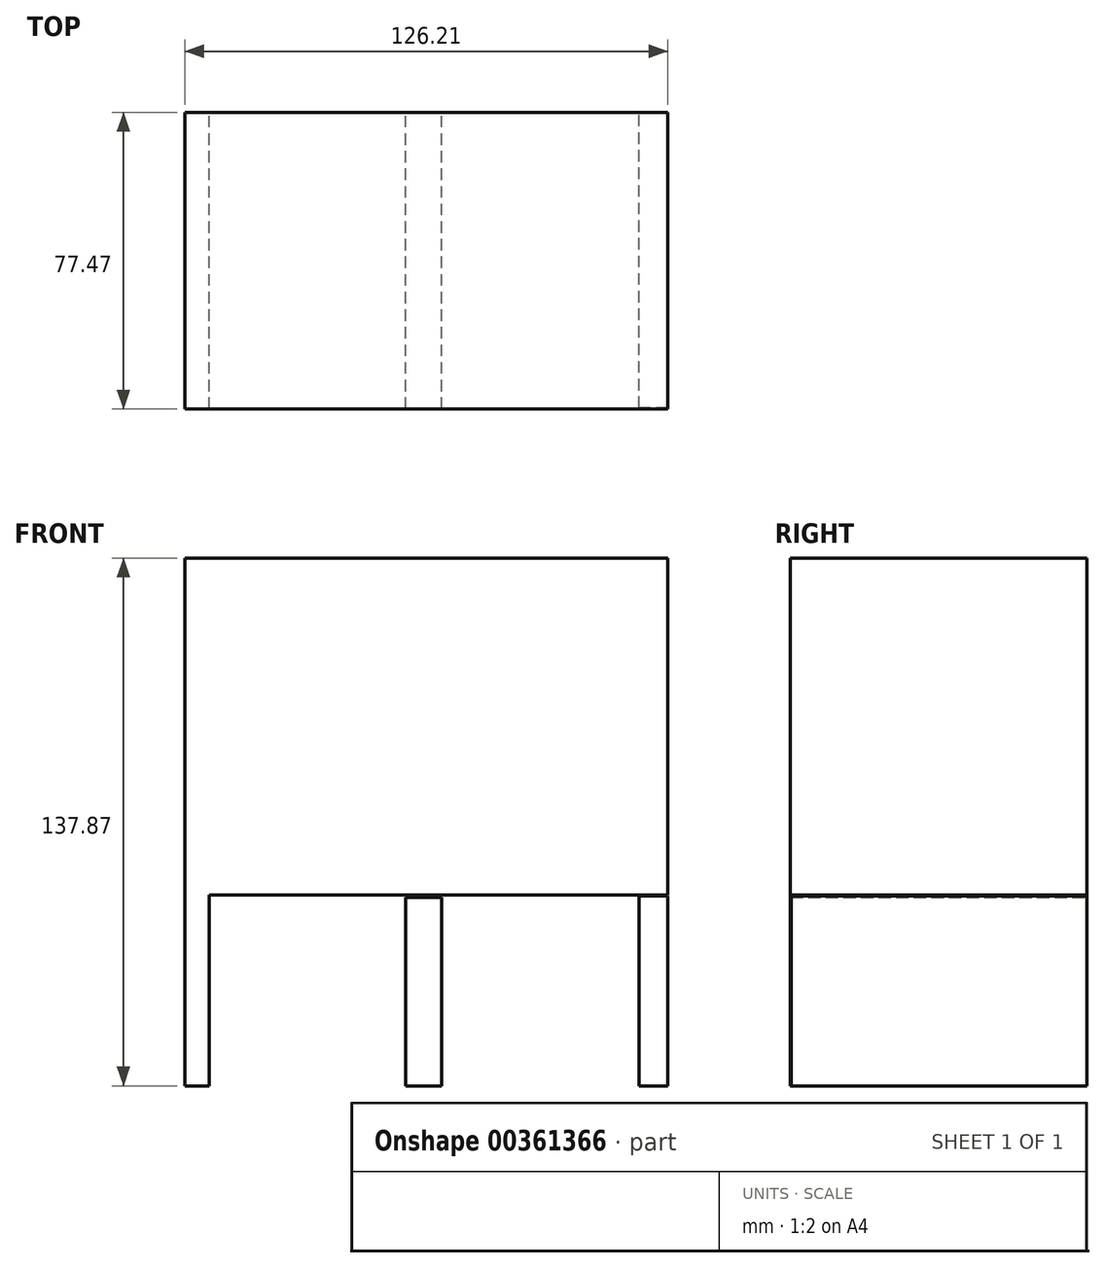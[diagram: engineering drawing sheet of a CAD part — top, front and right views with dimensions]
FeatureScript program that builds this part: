
annotation { "Feature Type Name" : "Feature", "Feature Type Description" : "" }
export const myFeature = defineFeature(function(context is Context, id is Id, definition is map)
    precondition{}
    {
        {
            var Q0;
            Q0=qCreatedBy(makeId("Front.planeOp"),FACE);
            var sketch = newSketch(context, id + "F0", { "sketchPlane" : qUnion([Q0])});
            skLineSegment(sketch, "E0.bottom", {"start": v(-62.38, 61.94) * mm, "end": v(63.83, 61.94) * mm});
            skLineSegment(sketch, "E0.top", {"start": v(-62.38, -26.09) * mm, "end": v(63.83, -26.09) * mm});
            skLineSegment(sketch, "E0.left", {"start": v(-62.38, 61.94) * mm, "end": v(-62.38, -26.09) * mm});
            skLineSegment(sketch, "E0.right", {"start": v(63.83, 61.94) * mm, "end": v(63.83, -26.09) * mm});
            skSolve(sketch);
        }
        {
            var Q0;
            Q0=makeQuery(id+"F0.imprint","IMPRINT",FACE,{"disambiguationData":[TD([[makeQuery(id+"F0.imprint","IMPRINT",EDGE,{"derivedFrom":sQuery(id+"F0.wireOp",EDGE,"E0.bottom")}),-1.0]])]});
            extrude(context, id + "F1", {"entities" : qUnion([Q0]), "depth" : 77.47 * mm});
        }
        {
            var Q0;
            Q0=qCreatedBy(makeId("Front.planeOp"),FACE);
            var sketch = newSketch(context, id + "F2", { "sketchPlane" : qUnion([Q0])});
            skLineSegment(sketch, "E1.bottom", {"start": v(-62.38, -26.09) * mm, "end": v(-55.96, -26.09) * mm});
            skLineSegment(sketch, "E1.top", {"start": v(-62.38, -75.93) * mm, "end": v(-55.96, -75.93) * mm});
            skLineSegment(sketch, "E1.left", {"start": v(-62.38, -26.09) * mm, "end": v(-62.38, -75.93) * mm});
            skLineSegment(sketch, "E1.right", {"start": v(-55.96, -26.09) * mm, "end": v(-55.96, -75.93) * mm});
            skLineSegment(sketch, "E2.bottom", {"start": v(63.83, -26.38) * mm, "end": v(56.25, -26.38) * mm});
            skLineSegment(sketch, "E2.top", {"start": v(63.83, -75.93) * mm, "end": v(56.25, -75.93) * mm});
            skLineSegment(sketch, "E2.left", {"start": v(63.83, -26.38) * mm, "end": v(63.83, -75.93) * mm});
            skLineSegment(sketch, "E2.right", {"start": v(56.25, -26.38) * mm, "end": v(56.25, -75.93) * mm});
            skLineSegment(sketch, "E3.bottom", {"start": v(-4.66, -26.67) * mm, "end": v(4.66, -26.67) * mm});
            skLineSegment(sketch, "E3.top", {"start": v(-4.66, -75.93) * mm, "end": v(4.66, -75.93) * mm});
            skLineSegment(sketch, "E3.left", {"start": v(-4.66, -26.67) * mm, "end": v(-4.66, -75.93) * mm});
            skLineSegment(sketch, "E3.right", {"start": v(4.66, -26.67) * mm, "end": v(4.66, -75.93) * mm});
            skSolve(sketch);
        }
        {
            var Q0;
            Q0=qCreatedBy(makeId("Front.planeOp"),FACE);
            var sketch = newSketch(context, id + "F3", { "sketchPlane" : qUnion([Q0])});
            skLineSegment(sketch, "E4", {"start": v(-55.67, -26.96) * mm, "end": v(-5.25, -75.93) * mm});
            skLineSegment(sketch, "E5", {"start": v(-55.96, -75.93) * mm, "end": v(-5.25, -26.38) * mm});
            skLineSegment(sketch, "E6", {"start": v(-5.25, -26.38) * mm, "end": v(4.96, -26.38) * mm});
            skLineSegment(sketch, "E7", {"start": v(4.96, -26.38) * mm, "end": v(56.25, -75.93) * mm});
            skLineSegment(sketch, "E8", {"start": v(56.25, -26.38) * mm, "end": v(4.96, -75.93) * mm});
            skSolve(sketch);
        }
        {
            var Q0;
            Q0=makeQuery(id+"F2.imprint","IMPRINT",FACE,{"disambiguationData":[TD([[makeQuery(id+"F2.imprint","IMPRINT",EDGE,{"derivedFrom":sQuery(id+"F2.wireOp",EDGE,"E1.bottom")}),-1.0]])]});
            extrude(context, id + "F4", {"entities" : qUnion([Q0]), "operationType" : NewBodyOperationType.ADD, "depth" : 77.47 * mm});
        }
        {
            var Q0;
            Q0=makeQuery(id+"F2.imprint","IMPRINT",FACE,{"disambiguationData":[TD([[makeQuery(id+"F2.imprint","IMPRINT",EDGE,{"derivedFrom":sQuery(id+"F2.wireOp",EDGE,"E3.bottom")}),-1.0]])]});
            extrude(context, id + "F5", {"entities" : qUnion([Q0]), "depth" : 77.47 * mm});
        }
        {
            var Q0;
            Q0=makeQuery(id+"F2.imprint","IMPRINT",FACE,{"disambiguationData":[TD([[makeQuery(id+"F2.imprint","IMPRINT",EDGE,{"derivedFrom":sQuery(id+"F2.wireOp",EDGE,"E2.bottom")}),1.0]])]});
            extrude(context, id + "F6", {"entities" : qUnion([Q0]), "depth" : 77.22 * mm});
        }
        {
            var Q0;
            Q0=sQuery(id+"F3.wireOp",EDGE,"E4");
            extrude(context, id + "F7", {"bodyType" : ToolBodyType.SURFACE, "surfaceEntities" : qUnion([Q0]), "depth" : 43.18 * mm});
        }
        {
            var Q0;
            Q0=sQuery(id+"F3.wireOp",EDGE,"E5");
            extrude(context, id + "F8", {"bodyType" : ToolBodyType.SURFACE, "surfaceEntities" : qUnion([Q0]), "depth" : 37.34 * mm});
        }
        {
            var Q0;
            Q0=sQuery(id+"F3.wireOp",EDGE,"E7");
            extrude(context, id + "F9", {"bodyType" : ToolBodyType.SURFACE, "surfaceEntities" : qUnion([Q0]), "depth" : 42.67 * mm});
        }
        {
            var Q0;
            Q0=sQuery(id+"F3.wireOp",EDGE,"E8");
            extrude(context, id + "F10", {"bodyType" : ToolBodyType.SURFACE, "surfaceEntities" : qUnion([Q0]), "depth" : 36.83 * mm});
        }
    });
